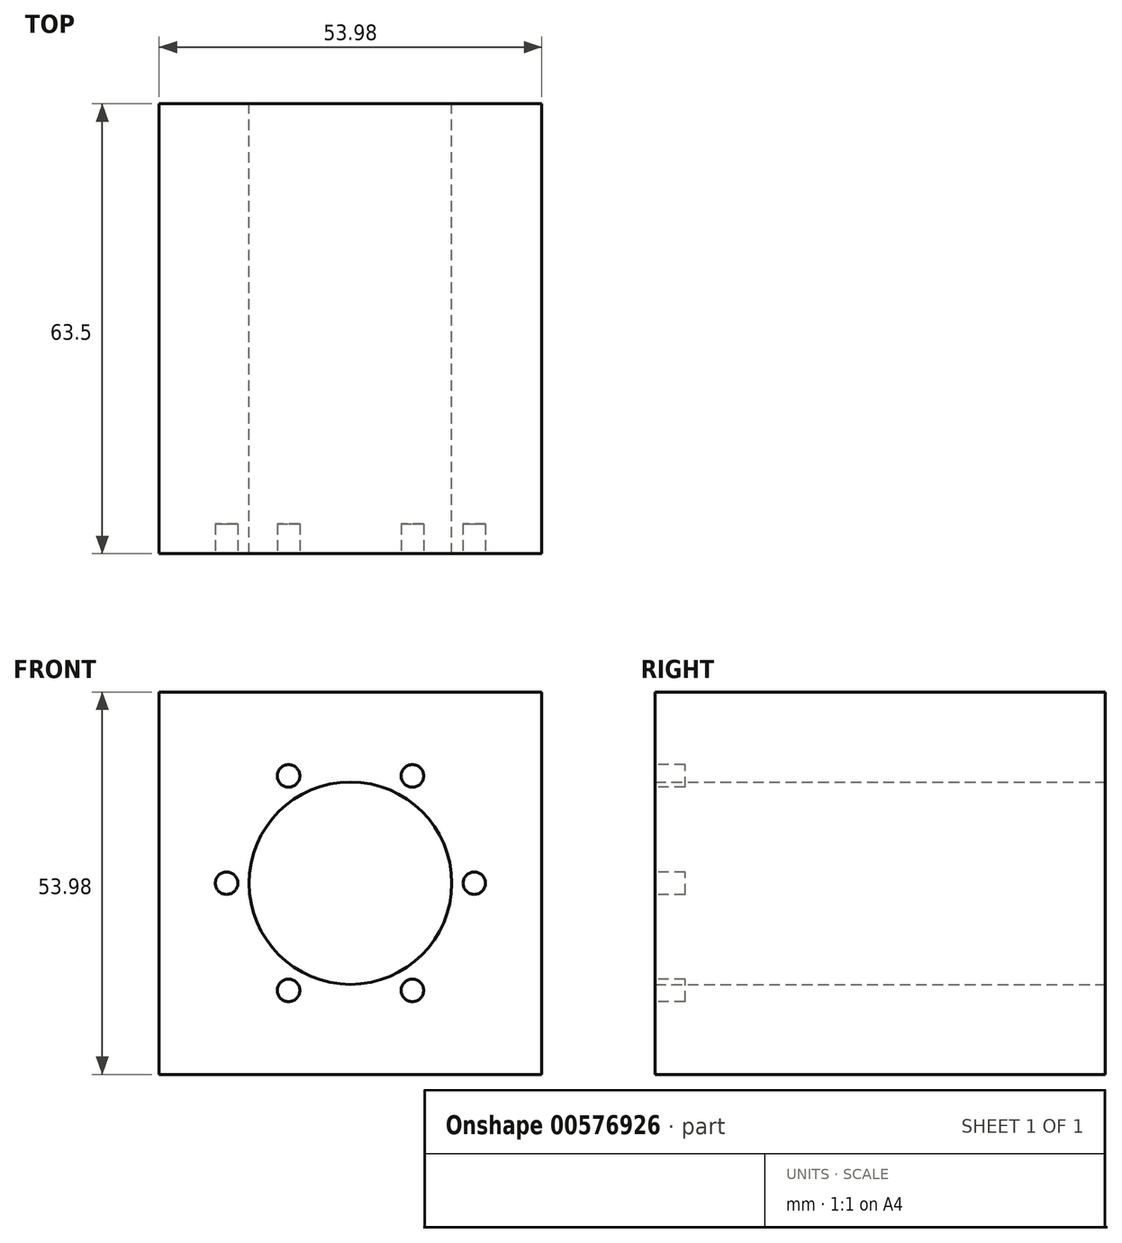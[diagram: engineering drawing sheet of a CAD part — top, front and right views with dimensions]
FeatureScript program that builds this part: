
annotation { "Feature Type Name" : "Feature", "Feature Type Description" : "" }
export const myFeature = defineFeature(function(context is Context, id is Id, definition is map)
    precondition{}
    {
        {
            var Q0;
            Q0=qCreatedBy(makeId("Front.planeOp"),FACE);
            var sketch = newSketch(context, id + "F0", { "sketchPlane" : qUnion([Q0])});
            skLineSegment(sketch, "E0.rect.bottom", {"start": v(26.99, -26.99) * mm, "end": v(-26.99, -26.99) * mm});
            skLineSegment(sketch, "E0.rect.top", {"start": v(26.99, 26.99) * mm, "end": v(-26.99, 26.99) * mm});
            skLineSegment(sketch, "E0.rect.left", {"start": v(26.99, -26.99) * mm, "end": v(26.99, 26.99) * mm});
            skLineSegment(sketch, "E0.rect.right", {"start": v(-26.99, -26.99) * mm, "end": v(-26.99, 26.99) * mm});
            skPoint(sketch, "E0.rect.middle", {"position": v(0, 0) * mm});
            skCircle(sketch, "E1", {"center": v(0, 0) * mm, "radius": 14.29 * mm});
            skSolve(sketch);
        }
        {
            var Q0;
            Q0=qSketchRegion(id+"F0",true);
            extrude(context, id + "F1", {"entities" : qUnion([Q0]), "endBound" : BoundingType.SYMMETRIC, "depth" : 63.5 * mm});
        }
        {
            var Q0;
            Q0=makeQuery(id+"F1.opExtrude","CAP_FACE",FACE,{"disambiguationData":[OSD([sQuery(id+"F0.wireOp",EDGE,"E0.rect.bottom"),sQuery(id+"F0.wireOp",EDGE,"E0.rect.top"),sQuery(id+"F0.wireOp",EDGE,"E0.rect.left"),sQuery(id+"F0.wireOp",EDGE,"E0.rect.right"),sQuery(id+"F0.wireOp",EDGE,"E1")])],"isStart":false});
            var sketch = newSketch(context, id + "F2", { "sketchPlane" : qUnion([Q0])});
            skCircle(sketch, "E2", {"center": v(-17.48, 0) * mm, "radius": 1.59 * mm});
            skCircle(sketch, "E3.1.0", {"center": v(-8.74, -15.13) * mm, "radius": 1.59 * mm});
            skCircle(sketch, "E3.2.0", {"center": v(8.74, -15.13) * mm, "radius": 1.59 * mm});
            skCircle(sketch, "E3.3.0", {"center": v(17.48, 0) * mm, "radius": 1.59 * mm});
            skCircle(sketch, "E3.4.0", {"center": v(8.74, 15.13) * mm, "radius": 1.59 * mm});
            skCircle(sketch, "E3.5.0", {"center": v(-8.74, 15.13) * mm, "radius": 1.59 * mm});
            skPoint(sketch, "E3.center", {"position": v(0, 0) * mm});
            skSolve(sketch);
        }
        {
            var Q0;
            Q0=qSketchRegion(id+"F2",true);
            extrude(context, id + "F3", {"entities" : qUnion([Q0]), "operationType" : NewBodyOperationType.REMOVE, "oppositeDirection" : true, "depth" : 4.22 * mm, "offsetDistance" : 25.4 * mm});
        }
    });
